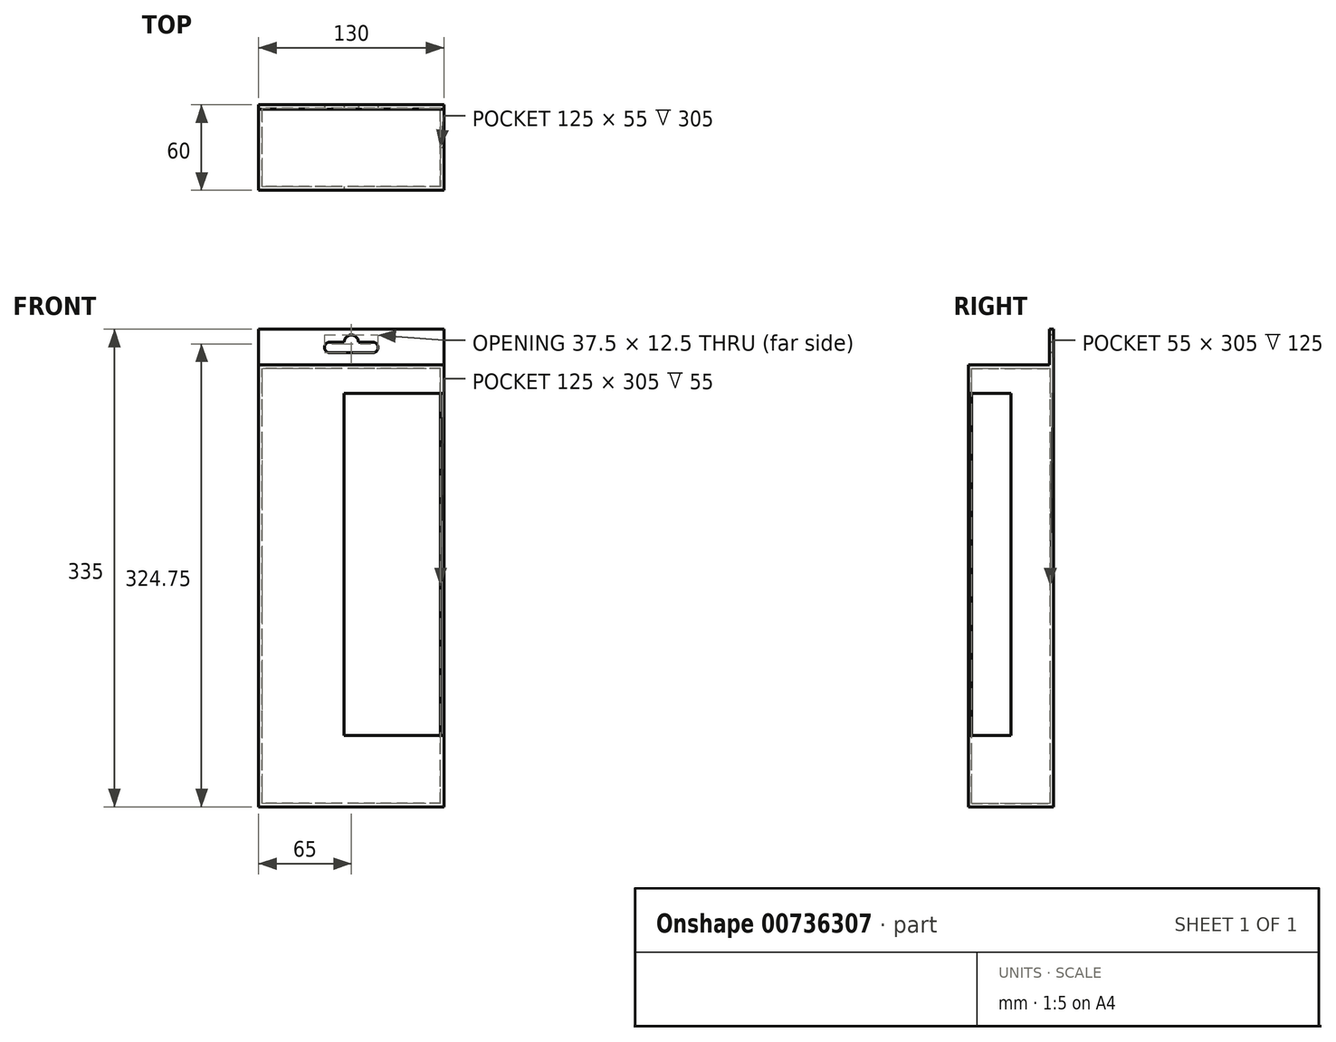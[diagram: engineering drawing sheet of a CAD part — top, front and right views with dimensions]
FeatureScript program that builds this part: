
annotation { "Feature Type Name" : "Feature", "Feature Type Description" : "" }
export const myFeature = defineFeature(function(context is Context, id is Id, definition is map)
    precondition{}
    {
        {
            var Q0;
            Q0=qCreatedBy(makeId("Front.planeOp"),FACE);
            var sketch = newSketch(context, id + "F0", { "sketchPlane" : qUnion([Q0])});
            skLineSegment(sketch, "E0.bottom", {"start": v(0, 0) * mm, "end": v(-130, 0) * mm});
            skLineSegment(sketch, "E0.top", {"start": v(0, 310) * mm, "end": v(-130, 310) * mm});
            skLineSegment(sketch, "E0.left", {"start": v(0, 0) * mm, "end": v(0, 310) * mm});
            skLineSegment(sketch, "E0.right", {"start": v(-130, 0) * mm, "end": v(-130, 310) * mm});
            skSolve(sketch);
        }
        {
            var Q0;
            Q0 = qSketchRegion(id + "F0", true);
            extrude(context, id + "F1", {"entities" : qUnion([Q0]), "depth" : 60 * mm, "offsetDistance" : 25 * mm});
        }
        {
            var Q0;
            Q0=makeQuery(id+"F1.opExtrude","CAP_FACE",FACE,{"disambiguationData":[OSD([sQuery(id+"F0.wireOp",EDGE,"E0.bottom"),sQuery(id+"F0.wireOp",EDGE,"E0.top"),sQuery(id+"F0.wireOp",EDGE,"E0.left"),sQuery(id+"F0.wireOp",EDGE,"E0.right")])],"isStart":false});
            var sketch = newSketch(context, id + "F2", { "sketchPlane" : qUnion([Q0])});
            skLineSegment(sketch, "E1", {"start": v(0, 310) * mm, "end": v(0, 290) * mm});
            skLineSegment(sketch, "E2.bottom", {"start": v(0, 290) * mm, "end": v(-70, 290) * mm});
            skLineSegment(sketch, "E2.top", {"start": v(0, 50) * mm, "end": v(-70, 50) * mm});
            skLineSegment(sketch, "E2.left", {"start": v(0, 290) * mm, "end": v(0, 50) * mm});
            skLineSegment(sketch, "E2.right", {"start": v(-70, 290) * mm, "end": v(-70, 50) * mm});
            skLineSegment(sketch, "E3", {"start": v(-48.13, 50) * mm, "end": v(-48.13, 0) * mm});
            skSolve(sketch);
        }
        {
            var Q0;
            Q0 = qSketchRegion(id + "F2", true);
            extrude(context, id + "F3", {"entities" : qUnion([Q0]), "operationType" : NewBodyOperationType.REMOVE, "oppositeDirection" : true, "depth" : 30 * mm, "offsetDistance" : 25 * mm});
        }
        {
            var Q0;
            Q0=makeQuery(id+"F3.boolean.opBoolean","COPY",FACE,{"derivedFrom":makeQuery(id+"F3.opExtrude","SWEPT_FACE",FACE,{"disambiguationData":[OSD([sQuery(id+"F2.wireOp",EDGE,"E2.top")])]})});
            var Q1;
            Q1=makeQuery(id+"F3.boolean.opBoolean","COPY",FACE,{"derivedFrom":makeQuery(id+"F3.opExtrude","SWEPT_FACE",FACE,{"disambiguationData":[OSD([sQuery(id+"F2.wireOp",EDGE,"E2.right")])]})});
            var Q2;
            Q2=makeQuery(id+"F3.boolean.opBoolean","COPY",FACE,{"derivedFrom":makeQuery(id+"F3.opExtrude","CAP_FACE",FACE,{"disambiguationData":[OSD([sQuery(id+"F2.wireOp",EDGE,"E2.bottom"),sQuery(id+"F2.wireOp",EDGE,"E2.top"),sQuery(id+"F2.wireOp",EDGE,"E2.left"),sQuery(id+"F2.wireOp",EDGE,"E2.right")])],"isStart":false})});
            var Q3;
            Q3=makeQuery(id+"F3.boolean.opBoolean","COPY",FACE,{"derivedFrom":makeQuery(id+"F3.opExtrude","SWEPT_FACE",FACE,{"disambiguationData":[OSD([sQuery(id+"F2.wireOp",EDGE,"E2.bottom")])]})});
            shell(context, id + "F4", {"entities" : qUnion([Q0, Q1, Q2, Q3]), "thickness" : 2.5 * mm});
        }
        {
            var Q0;
            Q0=makeQuery(id+"F1.opExtrude","SWEPT_FACE",FACE,{"disambiguationData":[OSD([sQuery(id+"F0.wireOp",EDGE,"E0.top")])]});
            var sketch = newSketch(context, id + "F5", { "sketchPlane" : qUnion([Q0])});
            skLineSegment(sketch, "E4.bottom", {"start": v(-130, 0) * mm, "end": v(0, 0) * mm});
            skLineSegment(sketch, "E4.top", {"start": v(-130, -3) * mm, "end": v(0, -3) * mm});
            skLineSegment(sketch, "E4.left", {"start": v(-130, 0) * mm, "end": v(-130, -3) * mm});
            skLineSegment(sketch, "E4.right", {"start": v(0, 0) * mm, "end": v(0, -3) * mm});
            skSolve(sketch);
        }
        {
            var Q0;
            Q0 = qSketchRegion(id + "F5", true);
            extrude(context, id + "F6", {"entities" : qUnion([Q0]), "operationType" : NewBodyOperationType.ADD, "depth" : 25 * mm, "offsetDistance" : 25 * mm});
        }
        {
            var Q0;
            Q0=makeQuery(id+"F6.opExtrude","CAP_EDGE",EDGE,{"disambiguationData":[OSD([sQuery(id+"F5.wireOp",EDGE,"E4.top")])],"isStart":false});
            var Q1;
            Q1=makeQuery(id+"F6.opExtrude","CAP_EDGE",EDGE,{"disambiguationData":[OSD([sQuery(id+"F5.wireOp",EDGE,"E4.bottom")])],"isStart":false});
            fillet(context, id + "F7", {"entities" : qUnion([Q0, Q1]), "radius" : 1.5 * mm, "tangentPropagation" : true, "allowEdgeOverflow" : false});
        }
        {
            var Q0;
            Q0=makeQuery(id+"F6.opExtrude","SWEPT_EDGE",EDGE,{"disambiguationData":[OSD([sQuery(id+"F0.wireOp",EDGE,"E0.top"),sQuery(id+"F0.wireOp",EDGE,"E0.left"),sQuery(id+"F5.wireOp",EDGE,"E4.top"),sQuery(id+"F5.wireOp",EDGE,"E4.right")])]});
            var Q1;
            Q1=makeQuery(id+"F6.opExtrude","SWEPT_EDGE",EDGE,{"disambiguationData":[OSD([sQuery(id+"F0.wireOp",EDGE,"E0.top"),sQuery(id+"F0.wireOp",EDGE,"E0.right"),sQuery(id+"F5.wireOp",EDGE,"E4.top"),sQuery(id+"F5.wireOp",EDGE,"E4.left")])]});
            fillet(context, id + "F8", {"entities" : qUnion([Q0, Q1]), "radius" : 1.5 * mm, "allowEdgeOverflow" : false});
        }
        {
            var Q0;
            Q0=makeQuery(id+"F6.opExtrude","SWEPT_FACE",FACE,{"disambiguationData":[OSD([sQuery(id+"F5.wireOp",EDGE,"E4.top")])]});
            var sketch = newSketch(context, id + "F9", { "sketchPlane" : qUnion([Q0])});
            skLineSegment(sketch, "E5", {"start": v(-60, 326) * mm, "end": v(-50, 326) * mm});
            skLineSegment(sketch, "E6.bottom", {"start": v(-50, 326) * mm, "end": v(-60, 326) * mm});
            skLineSegment(sketch, "E6.top", {"start": v(-50, 318.5) * mm, "end": v(-80, 318.5) * mm});
            skArc(sketch, "E7", {"start": v(-80, 326) * mm, "mid": v(-83.75, 322.25) * mm, "end": v(-80, 318.5) * mm});
            skArc(sketch, "E8", {"start": v(-50, 318.5) * mm, "mid": v(-46.25, 322.25) * mm, "end": v(-50, 326) * mm});
            skPoint(sketch, "E9.orphan", {"position": v(-82.5, 318.5) * mm});
            skLineSegment(sketch, "E10.trimOffspring", {"start": v(-70, 326) * mm, "end": v(-80, 326) * mm});
            skArc(sketch, "E11", {"start": v(-60, 326) * mm, "mid": v(-65, 331) * mm, "end": v(-70, 326) * mm});
            skSolve(sketch);
        }
        {
            var Q0;
            Q0 = qSketchRegion(id + "F9", true);
            extrude(context, id + "F10", {"entities" : qUnion([Q0]), "operationType" : NewBodyOperationType.REMOVE, "endBound" : BoundingType.THROUGH_ALL, "oppositeDirection" : true, "depth" : 25 * mm, "offsetDistance" : 25 * mm});
        }
        {
            var Q0;
            Q0 = qSketchRegion(id + "F5", true);
            extrude(context, id + "F11", {"entities" : qUnion([Q0]), "operationType" : NewBodyOperationType.ADD, "depth" : 25 * mm, "offsetDistance" : 25 * mm});
        }
        {
            var Q0;
            Q0 = qSketchRegion(id + "F9", true);
            extrude(context, id + "F12", {"entities" : qUnion([Q0]), "operationType" : NewBodyOperationType.REMOVE, "endBound" : BoundingType.THROUGH_ALL, "oppositeDirection" : true, "depth" : 25 * mm, "offsetDistance" : 25 * mm});
        }
    });
